# Revit family: Albardilla MACT. C-1
name_source: partatom
category: Modelos genéricos
units: mm (PartAtom-declared; Revit-internal decimal feet)

## family parameters
Compartido = No
Corte con vacíos al cargar = No
Cota de conector redondo = Diámetro de uso
Puede alojar armadura = No
Punto de cálculo de habitación = No
Se basa en plano de trabajo = No
Siempre vertical = No
Tipo de pieza = Normal

## types (6) — shared parameters
Descripción = Pieza de hormigón polímero con anclaje de acero inoxidable.
Fabricante = ULMA Architectural Solutions
Material = Hormigón polímero STONEO. Color C-1
URL = https://www.ulmaarchitectural.com
zero-valued in all types: Elevación por defecto

## per-type parameters (varying)
| type | Altura anclaje central | Ancho | Ancho doble | Ancho total | Modelo | Visibilidad dos filas | Visibilidad una fila |
| MACT14 | 41 mm  [stored 0.134514 ft] | 140 mm  [stored 0.459318 ft] | 35 mm  [stored 0.114829 ft] | 210 mm  [stored 0.688976 ft] | Albardilla MACT14 | No | Sí |
| MACT17 | 44 mm | 170 mm  [stored 0.557743 ft] | 43 mm | 240 mm  [stored 0.787402 ft] | Albardilla MACT17 | No | Sí |
| MACT22 | 47 mm  [stored 0.154199 ft] | 220 mm  [stored 0.721785 ft] | 55 mm  [stored 0.180446 ft] | 290 mm  [stored 0.951444 ft] | Albardilla MACT22 | No | Sí |
| MACT25 | 49 mm | 260 mm  [stored 0.853018 ft] | 65 mm  [stored 0.213255 ft] | 330 mm | Albardilla MACT25 | No | Sí |
| MACT30 | 51 mm | 310 mm  [stored 1.01706 ft] | 78 mm | 380 mm  [stored 1.24672 ft] | Albardilla MACT30 | Sí | No |
| MACT19 | 45 mm | 190 mm  [stored 0.62336 ft] | 48 mm | 260 mm  [stored 0.853018 ft] | Albardilla MACT19 | No | Sí |

note: column(s) folded — value = type name in every type: Código de montaje

note: [stored X ft] marks values corroborated as IEEE doubles in the binary element streams (Revit-internal decimal feet)
